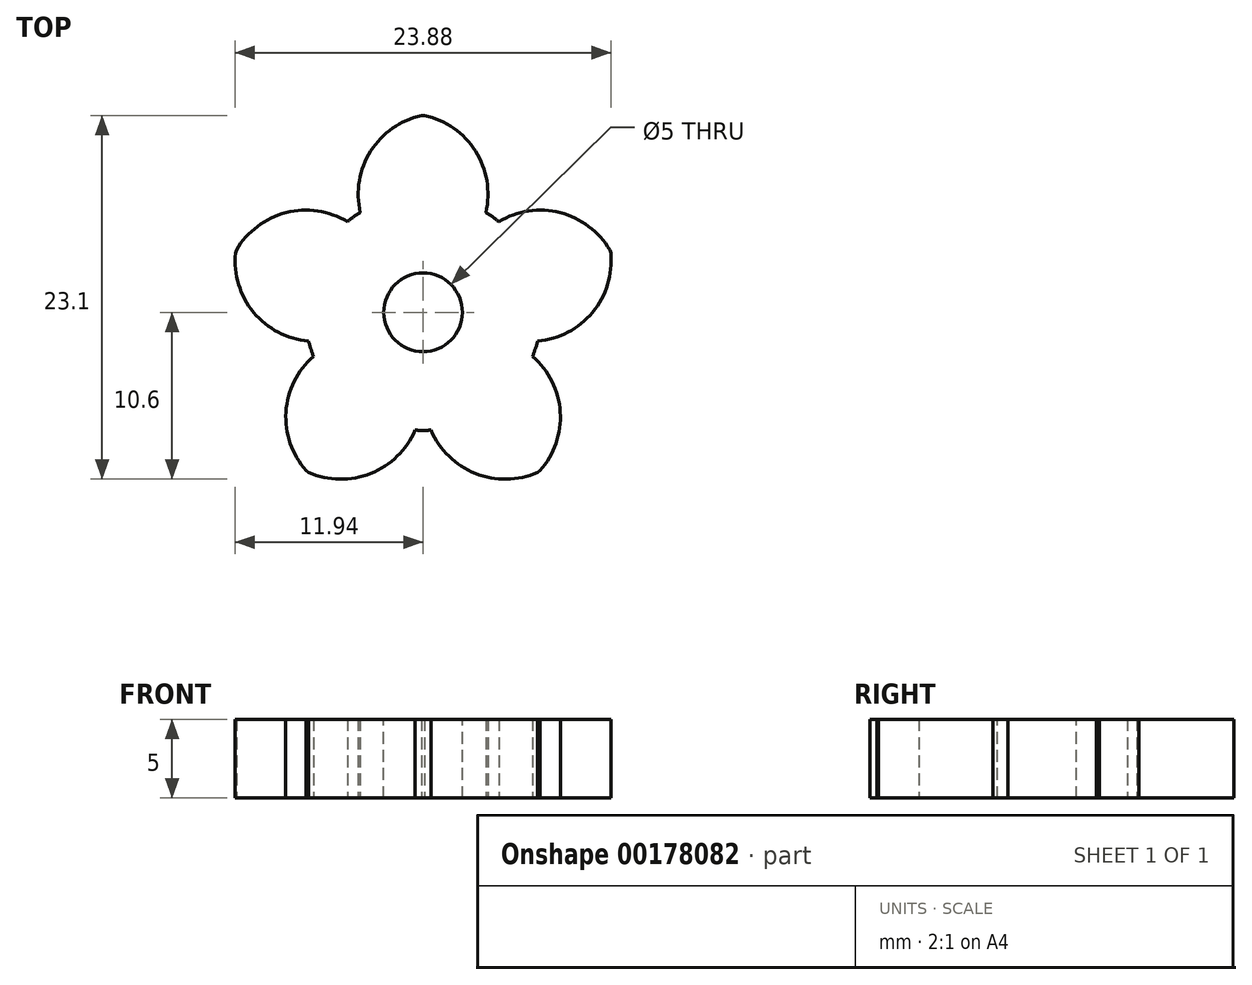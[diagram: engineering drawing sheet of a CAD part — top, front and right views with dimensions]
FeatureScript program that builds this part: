
annotation { "Feature Type Name" : "Feature", "Feature Type Description" : "" }
export const myFeature = defineFeature(function(context is Context, id is Id, definition is map)
    precondition{}
    {
        {
            var Q0;
            Q0=qCreatedBy(makeId("Top.planeOp"),FACE);
            var sketch = newSketch(context, id + "F0", { "sketchPlane" : qUnion([Q0])});
            skCircle(sketch, "E0", {"center": v(0, 0) * mm, "radius": 7.5 * mm});
            skLineSegment(sketch, "E1", {"start": v(0, 0) * mm, "end": v(0, 7.5) * mm, "construction": true});
            skLineSegment(sketch, "E2", {"start": v(0, 12.5) * mm, "end": v(-0.1, 12.5) * mm});
            skArc(sketch, "E3", {"start": v(-0.1, 12.5) * mm, "mid": v(-3.33, 10.24) * mm, "end": v(-3.99, 6.35) * mm});
            skArc(sketch, "E4.MirrorCS", {"start": v(0.1, 12.5) * mm, "mid": v(3.33, 10.24) * mm, "end": v(3.99, 6.35) * mm});
            skLineSegment(sketch, "E5.MirrorCS", {"start": v(0, 12.5) * mm, "end": v(0.1, 12.5) * mm});
            skArc(sketch, "E6.1.0", {"start": v(-11.92, 3.77) * mm, "mid": v(-10.76, 0) * mm, "end": v(-7.27, -1.83) * mm});
            skLineSegment(sketch, "E6.1.1", {"start": v(-11.89, 3.86) * mm, "end": v(-11.92, 3.77) * mm});
            skLineSegment(sketch, "E6.1.2", {"start": v(-11.89, 3.86) * mm, "end": v(-11.86, 3.96) * mm});
            skArc(sketch, "E6.1.3", {"start": v(-11.86, 3.96) * mm, "mid": v(-8.7, 6.33) * mm, "end": v(-4.8, 5.76) * mm});
            skArc(sketch, "E6.2.0", {"start": v(-7.27, -10.17) * mm, "mid": v(-3.33, -10.24) * mm, "end": v(-0.5, -7.48) * mm});
            skLineSegment(sketch, "E6.2.1", {"start": v(-7.35, -10.11) * mm, "end": v(-7.27, -10.17) * mm});
            skLineSegment(sketch, "E6.2.2", {"start": v(-7.35, -10.11) * mm, "end": v(-7.43, -10.05) * mm});
            skArc(sketch, "E6.2.3", {"start": v(-7.43, -10.05) * mm, "mid": v(-8.7, -6.33) * mm, "end": v(-6.96, -2.8) * mm});
            skArc(sketch, "E6.3.0", {"start": v(7.43, -10.05) * mm, "mid": v(8.7, -6.33) * mm, "end": v(6.96, -2.8) * mm});
            skLineSegment(sketch, "E6.3.1", {"start": v(7.35, -10.11) * mm, "end": v(7.43, -10.05) * mm});
            skLineSegment(sketch, "E6.3.2", {"start": v(7.35, -10.11) * mm, "end": v(7.27, -10.17) * mm});
            skArc(sketch, "E6.3.3", {"start": v(7.27, -10.17) * mm, "mid": v(3.33, -10.24) * mm, "end": v(0.5, -7.48) * mm});
            skArc(sketch, "E6.4.0", {"start": v(11.86, 3.96) * mm, "mid": v(8.7, 6.33) * mm, "end": v(4.8, 5.76) * mm});
            skLineSegment(sketch, "E6.4.1", {"start": v(11.89, 3.86) * mm, "end": v(11.86, 3.96) * mm});
            skLineSegment(sketch, "E6.4.2", {"start": v(11.89, 3.86) * mm, "end": v(11.92, 3.77) * mm});
            skArc(sketch, "E6.4.3", {"start": v(11.92, 3.77) * mm, "mid": v(10.76, 0) * mm, "end": v(7.27, -1.83) * mm});
            skSolve(sketch);
        }
        {
            var Q0;
            Q0 = qSketchRegion(id + "F0", true);
            extrude(context, id + "F1", {"entities" : qUnion([Q0]), "depth" : 5 * mm});
        }
        {
            var Q0;
            Q0=makeQuery(id+"F1.opExtrude","CAP_FACE",FACE,{"disambiguationData":[OSD([sQuery(id+"F0.wireOp",EDGE,"E0"),sQuery(id+"F0.wireOp",EDGE,"E2"),sQuery(id+"F0.wireOp",EDGE,"E3"),sQuery(id+"F0.wireOp",EDGE,"E4.MirrorCS"),sQuery(id+"F0.wireOp",EDGE,"E5.MirrorCS"),sQuery(id+"F0.wireOp",EDGE,"E6.1.0"),sQuery(id+"F0.wireOp",EDGE,"E6.1.1"),sQuery(id+"F0.wireOp",EDGE,"E6.1.2"),sQuery(id+"F0.wireOp",EDGE,"E6.1.3"),sQuery(id+"F0.wireOp",EDGE,"E6.2.0"),sQuery(id+"F0.wireOp",EDGE,"E6.2.1"),sQuery(id+"F0.wireOp",EDGE,"E6.2.2"),sQuery(id+"F0.wireOp",EDGE,"E6.2.3"),sQuery(id+"F0.wireOp",EDGE,"E6.3.0"),sQuery(id+"F0.wireOp",EDGE,"E6.3.1"),sQuery(id+"F0.wireOp",EDGE,"E6.3.2"),sQuery(id+"F0.wireOp",EDGE,"E6.3.3"),sQuery(id+"F0.wireOp",EDGE,"E6.4.0"),sQuery(id+"F0.wireOp",EDGE,"E6.4.1"),sQuery(id+"F0.wireOp",EDGE,"E6.4.2"),sQuery(id+"F0.wireOp",EDGE,"E6.4.3")])],"isStart":false});
            var sketch = newSketch(context, id + "F2", { "sketchPlane" : qUnion([Q0])});
            skCircle(sketch, "E7", {"center": v(0, 0) * mm, "radius": 2.5 * mm});
            skSolve(sketch);
        }
        {
            var Q0;
            Q0 = qSketchRegion(id + "F2", true);
            extrude(context, id + "F3", {"entities" : qUnion([Q0]), "operationType" : NewBodyOperationType.REMOVE, "endBound" : BoundingType.THROUGH_ALL, "oppositeDirection" : true, "depth" : 5 * mm});
        }
    });
